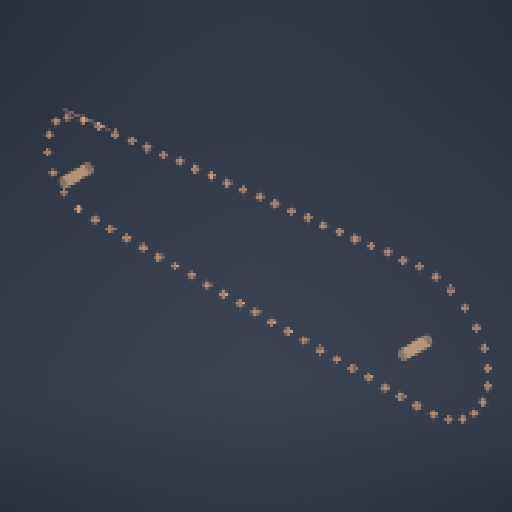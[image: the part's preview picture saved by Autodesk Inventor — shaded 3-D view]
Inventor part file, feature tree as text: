
AUTODESK INVENTOR PART (.ipt)
format: ipt  version: 2025.2 (Build 292293000, 293)  size: 146,944 bytes
history: native  units: in
note: dims shown in document units (in); Inventor stores cm internally (conversion verified against a paired STEP export)
features: other x65, extrude x2, pattern_linear x1
ambient origin geometry x8: Origin, YZ Plane, XZ Plane, XY Plane, X Axis, Y Axis, Z Axis, Center Point
bodies: Body1 (feature_tree), Body2 (feature_tree)
feature tree (68):
  other  "Work Point1"
  pattern_linear  "Rectangular Pattern1"  Spacing1=24.4788in  [1 undecoded]
  other  "Work Axis1"
  other  "Work Point2"
  other  "Work Point3"
  other  "Work Point4"
  other  "Work Point5"
  other  "Work Point6"
  other  "Work Point7"
  other  "Work Point8"
  other  "Work Point9"
  other  "Work Point10"
  other  "Work Point50"
  other  "Work Point51"
  other  "Work Point52"
  other  "Work Point53"
  other  "Work Point54"
  other  "Work Point55"
  other  "Work Point56"
  other  "Work Point57"
  other  "Work Point58"
  other  "Work Point59"
  other  "Work Point60"
  other  "Work Point61"
  other  "Work Point62"
  other  "Work Point63"
  other  "Work Point64"
  other  "Work Point65"
  other  "Work Point66"
  other  "Work Point67"
  other  "Work Point68"
  other  "Work Point69"
  other  "Work Point70"
  other  "Work Point71"
  other  "Work Point72"
  other  "Work Point73"
  other  "Work Point74"
  other  "Work Point75"
  other  "Work Point76"
  other  "Work Point77"
  other  "Work Point78"
  other  "Work Point79"
  other  "Work Point80"
  other  "Work Point81"
  other  "Work Point82"
  other  "Work Point83"
  other  "Srf1"
  other  "Srf2"
  other  "Work Point97"
  other  "Work Point98"
  other  "Work Point99"
  other  "Work Point100"
  other  "Work Point101"
  other  "Work Point102"
  other  "Work Point103"
  other  "Work Point104"
  other  "Work Point105"
  other  "Work Point106"
  other  "Work Point107"
  other  "Work Point108"
  other  "Work Point109"
  other  "Work Point110"
  other  "Work Point111"
  other  "Work Point112"
  other  "Work Point113"
  other  "Work Point114"
  extrude  "ExtrusionSrf1"  Depth=7.9856in
  extrude  "ExtrusionSrf2"  Depth=7.9856in
note: 1 required parameter value undecoded (feature->parameter linkage not recoverable at this tier; creation-order binding heuristic only, values carry confidence <= 0.55)
